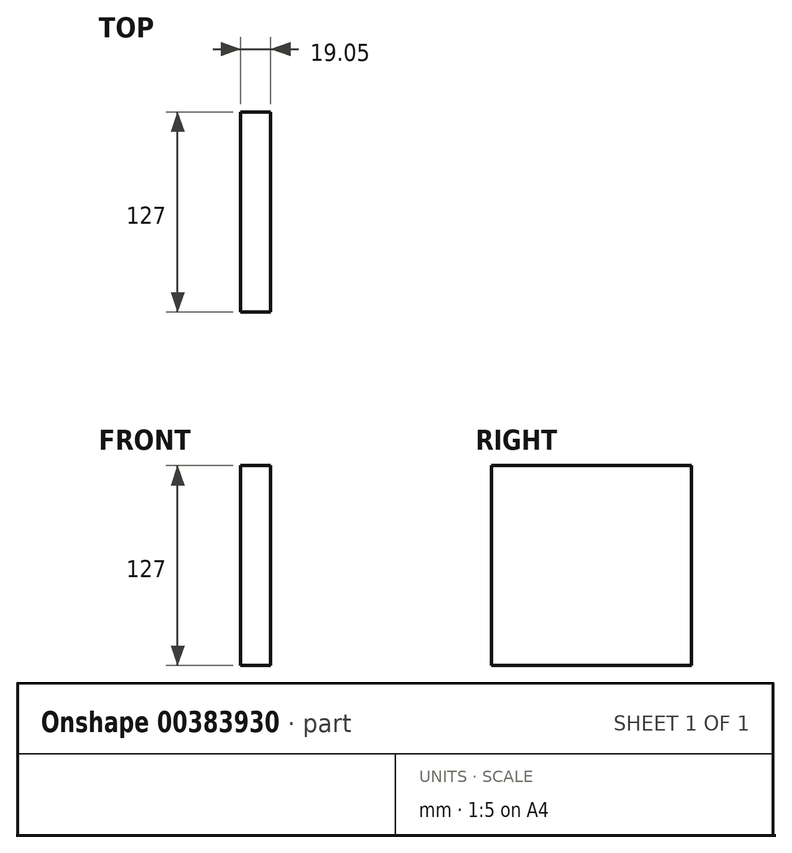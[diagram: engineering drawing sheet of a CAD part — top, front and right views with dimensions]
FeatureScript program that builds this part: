
annotation { "Feature Type Name" : "Feature", "Feature Type Description" : "" }
export const myFeature = defineFeature(function(context is Context, id is Id, definition is map)
    precondition{}
    {
        {
            var Q0;
            Q0=qCreatedBy(makeId("Right.planeOp"),FACE);
            var sketch = newSketch(context, id + "F0", { "sketchPlane" : qUnion([Q0])});
            skLineSegment(sketch, "E0.bottom", {"start": v(-74.68, 91) * mm, "end": v(52.32, 91) * mm});
            skLineSegment(sketch, "E0.top", {"start": v(-74.68, -36) * mm, "end": v(52.32, -36) * mm});
            skLineSegment(sketch, "E0.left", {"start": v(-74.68, 91) * mm, "end": v(-74.68, -36) * mm});
            skLineSegment(sketch, "E0.right", {"start": v(52.32, 91) * mm, "end": v(52.32, -36) * mm});
            skSolve(sketch);
        }
        {
            var Q0;
            Q0=makeQuery(id+"F0.imprint","IMPRINT",FACE,{"disambiguationData":[TD([[makeQuery(id+"F0.imprint","IMPRINT",EDGE,{"derivedFrom":sQuery(id+"F0.wireOp",EDGE,"E0.bottom")}),-1.0]])]});
            extrude(context, id + "F1", {"entities" : qUnion([Q0]), "depth" : 19.05 * mm});
        }
    });
